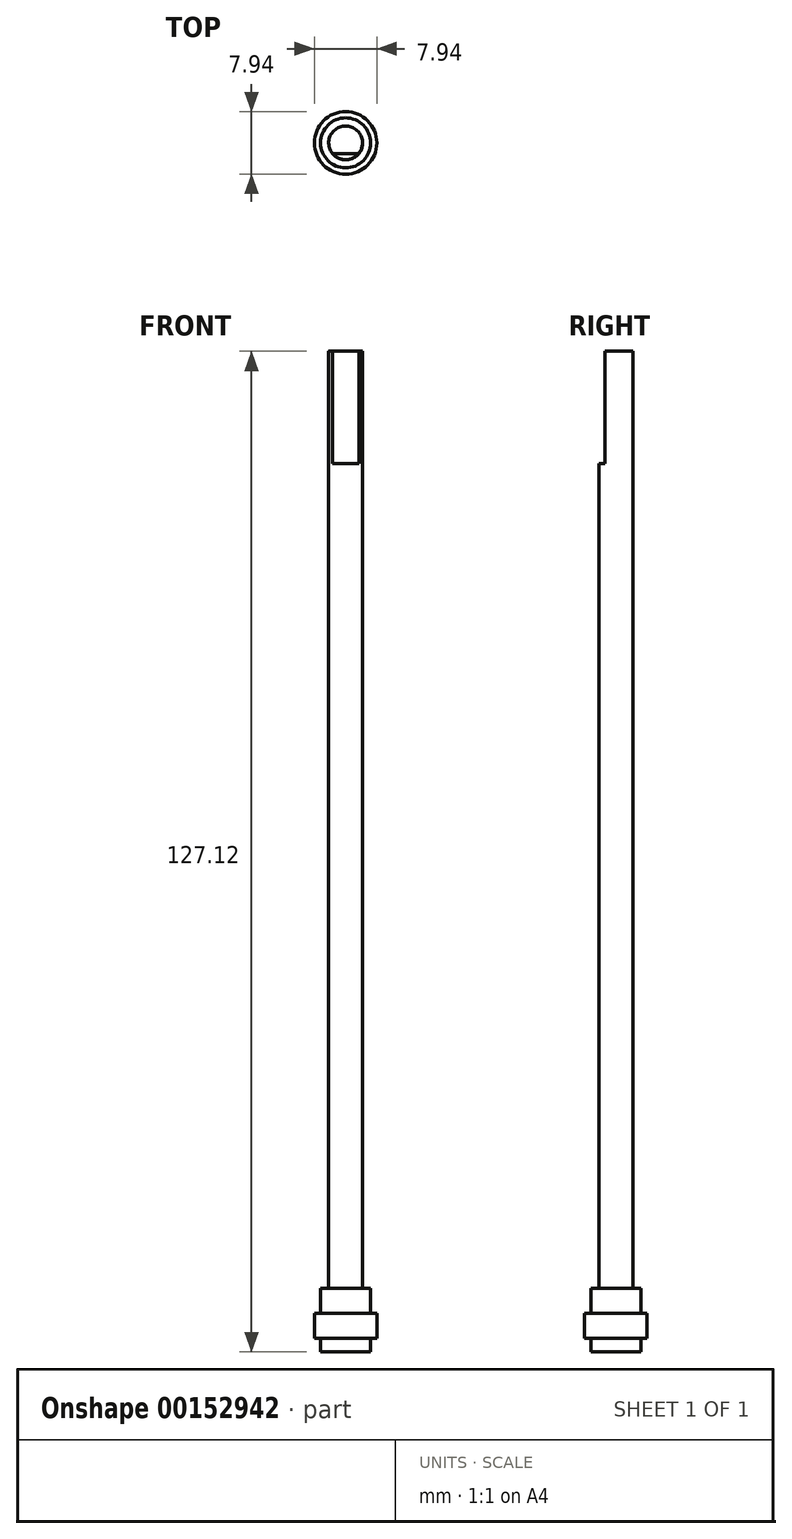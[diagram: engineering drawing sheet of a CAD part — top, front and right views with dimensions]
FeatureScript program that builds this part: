
annotation { "Feature Type Name" : "Feature", "Feature Type Description" : "" }
export const myFeature = defineFeature(function(context is Context, id is Id, definition is map)
    precondition{}
    {
        {
            var Q0;
            Q0=qCreatedBy(makeId("Top.planeOp"),FACE);
            var sketch = newSketch(context, id + "F0", { "sketchPlane" : qUnion([Q0])});
            skCircle(sketch, "E0", {"center": v(0, 0) * mm, "radius": 3.18 * mm});
            skSolve(sketch);
        }
        {
            var Q0;
            Q0=qSketchRegion(id+"F0",true);
            extrude(context, id + "F1", {"entities" : qUnion([Q0]), "depth" : 1.7 * mm});
        }
        {
            var Q0;
            Q0=makeQuery(id+"F1.opExtrude","CAP_FACE",FACE,{"disambiguationData":[OSD([sQuery(id+"F0.wireOp",EDGE,"E0")])],"isStart":false});
            var sketch = newSketch(context, id + "F2", { "sketchPlane" : qUnion([Q0])});
            skCircle(sketch, "E1", {"center": v(0, 0) * mm, "radius": 3.97 * mm});
            skSolve(sketch);
        }
        {
            var Q0;
            Q0=qSketchRegion(id+"F2",true);
            extrude(context, id + "F3", {"entities" : qUnion([Q0]), "operationType" : NewBodyOperationType.ADD, "depth" : 3.17 * mm});
        }
        {
            var Q0;
            Q0=makeQuery(id+"F3.opExtrude","CAP_FACE",FACE,{"disambiguationData":[OSD([sQuery(id+"F2.wireOp",EDGE,"E1")])],"isStart":false});
            var sketch = newSketch(context, id + "F4", { "sketchPlane" : qUnion([Q0])});
            skCircle(sketch, "E2", {"center": v(0, 0) * mm, "radius": 3.18 * mm});
            skSolve(sketch);
        }
        {
            var Q0;
            Q0=qSketchRegion(id+"F4",true);
            extrude(context, id + "F5", {"entities" : qUnion([Q0]), "operationType" : NewBodyOperationType.ADD, "depth" : 3.17 * mm});
        }
        {
            var Q0;
            Q0=makeQuery(id+"F5.opExtrude","CAP_FACE",FACE,{"disambiguationData":[OSD([sQuery(id+"F4.wireOp",EDGE,"E2")])],"isStart":false});
            var sketch = newSketch(context, id + "F6", { "sketchPlane" : qUnion([Q0])});
            skCircle(sketch, "E3", {"center": v(0, 0) * mm, "radius": 2.15 * mm});
            skSolve(sketch);
        }
        {
            var Q0;
            Q0=qSketchRegion(id+"F6",true);
            extrude(context, id + "F7", {"entities" : qUnion([Q0]), "operationType" : NewBodyOperationType.ADD, "depth" : 119.06 * mm});
        }
        {
            var Q0;
            Q0=makeQuery(id+"F7.opExtrude","CAP_FACE",FACE,{"disambiguationData":[OSD([sQuery(id+"F6.wireOp",EDGE,"E3")])],"isStart":false});
            var sketch = newSketch(context, id + "F8", { "sketchPlane" : qUnion([Q0])});
            skLineSegment(sketch, "E4.bottom", {"start": v(1.67, -1.36) * mm, "end": v(-1.67, -1.36) * mm});
            skLineSegment(sketch, "E4.top", {"start": v(1.67, -2.15) * mm, "end": v(-1.67, -2.15) * mm});
            skLineSegment(sketch, "E4.left", {"start": v(1.67, -1.36) * mm, "end": v(1.67, -2.15) * mm});
            skLineSegment(sketch, "E4.right", {"start": v(-1.67, -1.36) * mm, "end": v(-1.67, -2.15) * mm});
            skSolve(sketch);
        }
        {
            var Q0;
            Q0=qSketchRegion(id+"F8",true);
            extrude(context, id + "F9", {"entities" : qUnion([Q0]), "operationType" : NewBodyOperationType.REMOVE, "oppositeDirection" : true, "depth" : 14.29 * mm});
        }
    });
